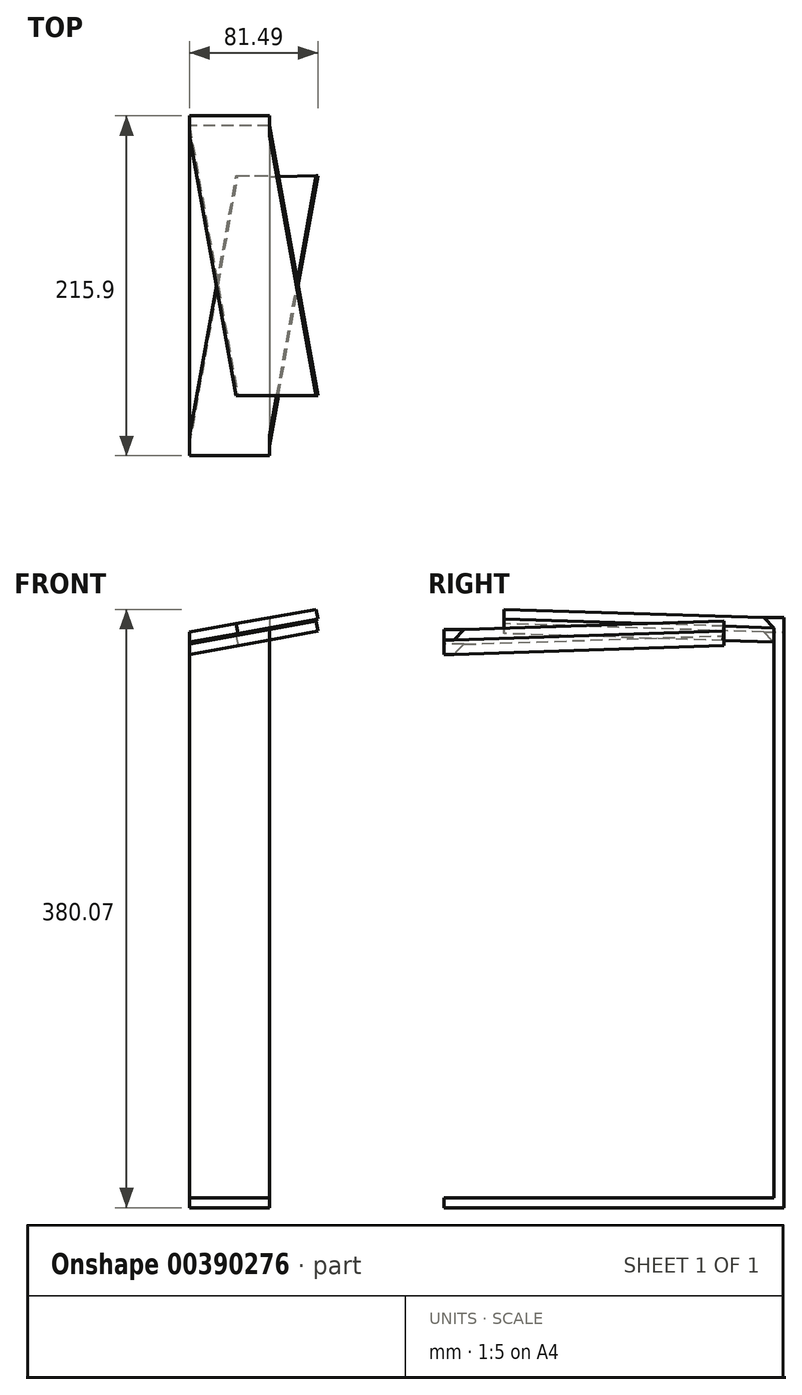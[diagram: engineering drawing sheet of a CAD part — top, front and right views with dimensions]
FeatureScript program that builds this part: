
annotation { "Feature Type Name" : "Feature", "Feature Type Description" : "" }
export const myFeature = defineFeature(function(context is Context, id is Id, definition is map)
    precondition{}
    {
        {
            var Q0;
            Q0=qCreatedBy(makeId("Front.planeOp"),FACE);
            var sketch = newSketch(context, id + "F0", { "sketchPlane" : qUnion([Q0])});
            skLineSegment(sketch, "E0.bottom", {"start": v(-25.4, 254) * mm, "end": v(25.4, 254) * mm});
            skLineSegment(sketch, "E0.top", {"start": v(-25.4, -254) * mm, "end": v(25.4, -254) * mm});
            skLineSegment(sketch, "E0.left", {"start": v(-25.4, 254) * mm, "end": v(-25.4, -254) * mm});
            skLineSegment(sketch, "E0.right", {"start": v(25.4, 254) * mm, "end": v(25.4, -254) * mm});
            skPoint(sketch, "E0.middle", {"position": v(0, 0) * mm});
            skLineSegment(sketch, "E1.left", {"start": v(-25.4, -254) * mm, "end": v(-25.4, -247.65) * mm});
            skLineSegment(sketch, "E1.right", {"start": v(25.4, -254) * mm, "end": v(25.4, -247.65) * mm});
            skLineSegment(sketch, "E2.top", {"start": v(-25.4, -260.35) * mm, "end": v(25.4, -260.35) * mm});
            skLineSegment(sketch, "E2.left", {"start": v(-25.4, -254) * mm, "end": v(-25.4, -260.35) * mm});
            skLineSegment(sketch, "E2.right", {"start": v(25.4, -254) * mm, "end": v(25.4, -260.35) * mm});
            skLineSegment(sketch, "E3", {"start": v(-25.4, 91.07) * mm, "end": v(25.4, 100.3) * mm});
            skLineSegment(sketch, "E4", {"start": v(-25.4, 97.52) * mm, "end": v(25.4, 106.76) * mm});
            skSolve(sketch);
        }
        {
            var Q0;
            {var subQ0=sQuery(id+"F0.wireOp",EDGE,"E1.left");Q0=makeQuery(id+"F0.imprint","IMPRINT",FACE,{"disambiguationData":[TD([[makeQuery(id+"F0.imprint","IMPRINT",EDGE,{"derivedFrom":subQ0}),-1.0]])]});}
            var Q1;
            {var subQ0=sQuery(id+"F0.wireOp",EDGE,"E3");Q1=makeQuery(id+"F0.imprint","IMPRINT",FACE,{"disambiguationData":[TD([[makeQuery(id+"F0.imprint","IMPRINT",EDGE,{"derivedFrom":subQ0}),1.0]])]});}
            extrude(context, id + "F1", {"entities" : qUnion([Q0, Q1]), "oppositeDirection" : true, "depth" : 6.35 * mm, "offsetDistance" : 25.4 * mm});
        }
        {
            var Q0;
            Q0=makeQuery(id+"F0.imprint","IMPRINT",FACE,{"disambiguationData":[TD([[makeQuery(id+"F0.imprint","IMPRINT",EDGE,{"derivedFrom":sQuery(id+"F0.wireOp",EDGE,"E0.top")}),-1.0]])]});
            extrude(context, id + "F2", {"entities" : qUnion([Q0]), "operationType" : NewBodyOperationType.ADD, "oppositeDirection" : true, "depth" : 215.9 * mm, "offsetDistance" : 25.4 * mm});
        }
        {
            var Q0;
            Q0=makeQuery(id+"F2.opExtrude","SWEPT_FACE",FACE,{"disambiguationData":[OSD([sQuery(id+"F0.wireOp",EDGE,"E2.top")])]});
            var sketch = newSketch(context, id + "F3", { "sketchPlane" : qUnion([Q0])});
            skLineSegment(sketch, "E5.bottom", {"start": v(25.4, -215.9) * mm, "end": v(-25.4, -215.9) * mm});
            skLineSegment(sketch, "E5.top", {"start": v(25.4, -209.55) * mm, "end": v(-25.4, -209.55) * mm});
            skLineSegment(sketch, "E5.left", {"start": v(25.4, -215.9) * mm, "end": v(25.4, -209.55) * mm});
            skLineSegment(sketch, "E5.right", {"start": v(-25.4, -215.9) * mm, "end": v(-25.4, -209.55) * mm});
            skSolve(sketch);
        }
        {
            var Q0;
            Q0=makeQuery(id+"F3.imprint","IMPRINT",FACE,{"disambiguationData":[TD([[makeQuery(id+"F3.imprint","IMPRINT",EDGE,{"derivedFrom":sQuery(id+"F3.wireOp",EDGE,"E5.bottom")}),1.0]])]});
            extrude(context, id + "F4", {"entities" : qUnion([Q0]), "operationType" : NewBodyOperationType.ADD, "oppositeDirection" : true, "depth" : 558.8 * mm, "offsetDistance" : 25.4 * mm});
        }
        {
            var Q0;
            {var subQ0=sQuery(id+"F0.wireOp",EDGE,"E3");Q0=makeQuery(id+"F0.imprint","IMPRINT",FACE,{"disambiguationData":[TD([[makeQuery(id+"F0.imprint","IMPRINT",EDGE,{"derivedFrom":subQ0}),1.0]])]});}
            extrude(context, id + "F5", {"entities" : qUnion([Q0]), "operationType" : NewBodyOperationType.ADD, "oppositeDirection" : true, "depth" : 177.8 * mm, "offsetDistance" : 25.4 * mm});
        }
        {
            var Q0;
            Q0=makeQuery(id+"F4.boolean.opBoolean","MERGE",FACE,{"derivedFrom":[makeQuery(id+"F2.opExtrude","CAP_FACE",FACE,{"disambiguationData":[OSD([sQuery(id+"F0.wireOp",EDGE,"E0.top"),sQuery(id+"F0.wireOp",EDGE,"E2.top"),sQuery(id+"F0.wireOp",EDGE,"E2.left"),sQuery(id+"F0.wireOp",EDGE,"E2.right")])],"isStart":false}),makeQuery(id+"F4.opExtrude","SWEPT_FACE",FACE,{"disambiguationData":[OSD([sQuery(id+"F3.wireOp",EDGE,"E5.bottom")])]})]});
            var sketch = newSketch(context, id + "F6", { "sketchPlane" : qUnion([Q0])});
            skLineSegment(sketch, "E6", {"start": v(25.4, 98.8) * mm, "end": v(-25.4, 107.95) * mm});
            skLineSegment(sketch, "E7", {"start": v(-25.4, 114.4) * mm, "end": v(25.4, 105.26) * mm});
            skSolve(sketch);
        }
        {
            var Q0;
            {var subQ0=sQuery(id+"F6.wireOp",EDGE,"E7");Q0=makeQuery(id+"F6.imprint","IMPRINT",FACE,{"disambiguationData":[TD([[makeQuery(id+"F6.imprint","IMPRINT",EDGE,{"derivedFrom":subQ0}),1.0]])]});}
            extrude(context, id + "F7", {"entities" : qUnion([Q0]), "operationType" : NewBodyOperationType.REMOVE, "oppositeDirection" : true, "depth" : 6.35 * mm, "offsetDistance" : 25.4 * mm});
        }
        {
            var Q0;
            {var subQ0=sQuery(id+"F6.wireOp",EDGE,"E6");Q0=makeQuery(id+"F6.imprint","IMPRINT",FACE,{"disambiguationData":[TD([[makeQuery(id+"F6.imprint","IMPRINT",EDGE,{"derivedFrom":subQ0}),-1.0]])]});}
            extrude(context, id + "F8", {"entities" : qUnion([Q0]), "operationType" : NewBodyOperationType.ADD, "oppositeDirection" : true, "depth" : 177.8 * mm, "offsetDistance" : 25.4 * mm});
        }
        {
            var Q0;
            Q0=makeQuery(id+"F5.opExtrude","SWEPT_FACE",FACE,{"disambiguationData":[OSD([sQuery(id+"F0.wireOp",EDGE,"E3")])]});
            var sketch = newSketch(context, id + "F9", { "sketchPlane" : qUnion([Q0])});
            skLineSegment(sketch, "E8", {"start": v(-8.7, -6.35) * mm, "end": v(22.34, -176.93) * mm});
            skLineSegment(sketch, "E9", {"start": v(42.94, -6.35) * mm, "end": v(75.54, -185.58) * mm});
            skLineSegment(sketch, "E10", {"start": v(22.34, -176.93) * mm, "end": v(74.13, -177.8) * mm});
            skSolve(sketch);
        }
        {
            var Q0;
            {var subQ0=sQuery(id+"F9.wireOp",EDGE,"E9");var subQ5=sQuery(id+"F9.wireOp",EDGE,"E10");var subQ6=makeQuery(id+"F9.imprint","INTERSECT",VERTEX,{"derivedFrom":[subQ0,subQ5]});Q0=makeQuery(id+"F9.imprint","IMPRINT",FACE,{"disambiguationData":[TD([[makeQuery(id+"F9.imprint","IMPRINT",EDGE,{"disambiguationData":[TD([[subQ6,1.0]])],"derivedFrom":subQ5}),1.0]])]});}
            extrude(context, id + "F10", {"entities" : qUnion([Q0]), "operationType" : NewBodyOperationType.ADD, "oppositeDirection" : true, "depth" : 6.35 * mm, "offsetDistance" : 25.4 * mm});
        }
        {
            var Q0;
            {var subQ3=sQuery(id+"F9.wireOp",EDGE,"E8");Q0=makeQuery(id+"F9.imprint","IMPRINT",FACE,{"disambiguationData":[TD([[makeQuery(id+"F9.imprint","IMPRINT",EDGE,{"derivedFrom":subQ3}),-1.0]])]});}
            var sketch = newSketch(context, id + "F11", { "sketchPlane" : qUnion([Q0])});
            skLineSegment(sketch, "E11", {"start": v(-8.7, -6.36) * mm, "end": v(22.53, -177.8) * mm});
            skLineSegment(sketch, "E12", {"start": v(22.53, -177.8) * mm, "end": v(-8.7, -177.8) * mm});
            skLineSegment(sketch, "E13", {"start": v(-8.7, -177.8) * mm, "end": v(-8.7, -6.36) * mm});
            skSolve(sketch);
        }
        {
            var Q0;
            Q0 = qSketchRegion(id + "F11", true);
            extrude(context, id + "F12", {"entities" : qUnion([Q0]), "operationType" : NewBodyOperationType.REMOVE, "oppositeDirection" : true, "depth" : 6.35 * mm, "offsetDistance" : 25.4 * mm});
        }
        {
            var Q0;
            Q0=makeQuery(id+"F8.opExtrude","SWEPT_FACE",FACE,{"disambiguationData":[OSD([sQuery(id+"F6.wireOp",EDGE,"E6")])]});
            var sketch = newSketch(context, id + "F13", { "sketchPlane" : qUnion([Q0])});
            skLineSegment(sketch, "E14", {"start": v(-7.5, -209.55) * mm, "end": v(23.7, -38.1) * mm});
            skLineSegment(sketch, "E15", {"start": v(44.12, -209.55) * mm, "end": v(76.33, -32.5) * mm});
            skLineSegment(sketch, "E16", {"start": v(23.7, -38.1) * mm, "end": v(75.3, -38.1) * mm});
            skLineSegment(sketch, "E17", {"start": v(23.7, -38.1) * mm, "end": v(-7.5, -38.1) * mm});
            skLineSegment(sketch, "E18", {"start": v(-7.5, -38.1) * mm, "end": v(-7.5, -209.55) * mm});
            skSolve(sketch);
        }
        {
            var Q0;
            {var subQ1=sQuery(id+"F6.wireOp",EDGE,"E6");var subQ2=makeQuery(id+"F8.opExtrude","SWEPT_EDGE",EDGE,{"disambiguationData":[OSD([sQuery(id+"F0.wireOp",EDGE,"E2.right"),sQuery(id+"F3.wireOp",EDGE,"E5.bottom"),sQuery(id+"F3.wireOp",EDGE,"E5.left"),subQ1])]});Q0=makeQuery(id+"F13.imprint","IMPRINT",FACE,{"disambiguationData":[TD([[makeQuery(id+"F13.imprint","IMPRINT",EDGE,{"derivedFrom":subQ2}),1.0]])]});}
            extrude(context, id + "F14", {"entities" : qUnion([Q0]), "operationType" : NewBodyOperationType.ADD, "oppositeDirection" : true, "depth" : 6.35 * mm, "offsetDistance" : 25.4 * mm});
        }
        {
            var Q0;
            Q0=makeQuery(id+"F13.imprint","IMPRINT",FACE,{"disambiguationData":[TD([[makeQuery(id+"F13.imprint","IMPRINT",EDGE,{"derivedFrom":sQuery(id+"F13.wireOp",EDGE,"E14")}),1.0]])]});
            extrude(context, id + "F15", {"entities" : qUnion([Q0]), "operationType" : NewBodyOperationType.REMOVE, "oppositeDirection" : true, "depth" : 6.35 * mm, "offsetDistance" : 25.4 * mm});
        }
    });
